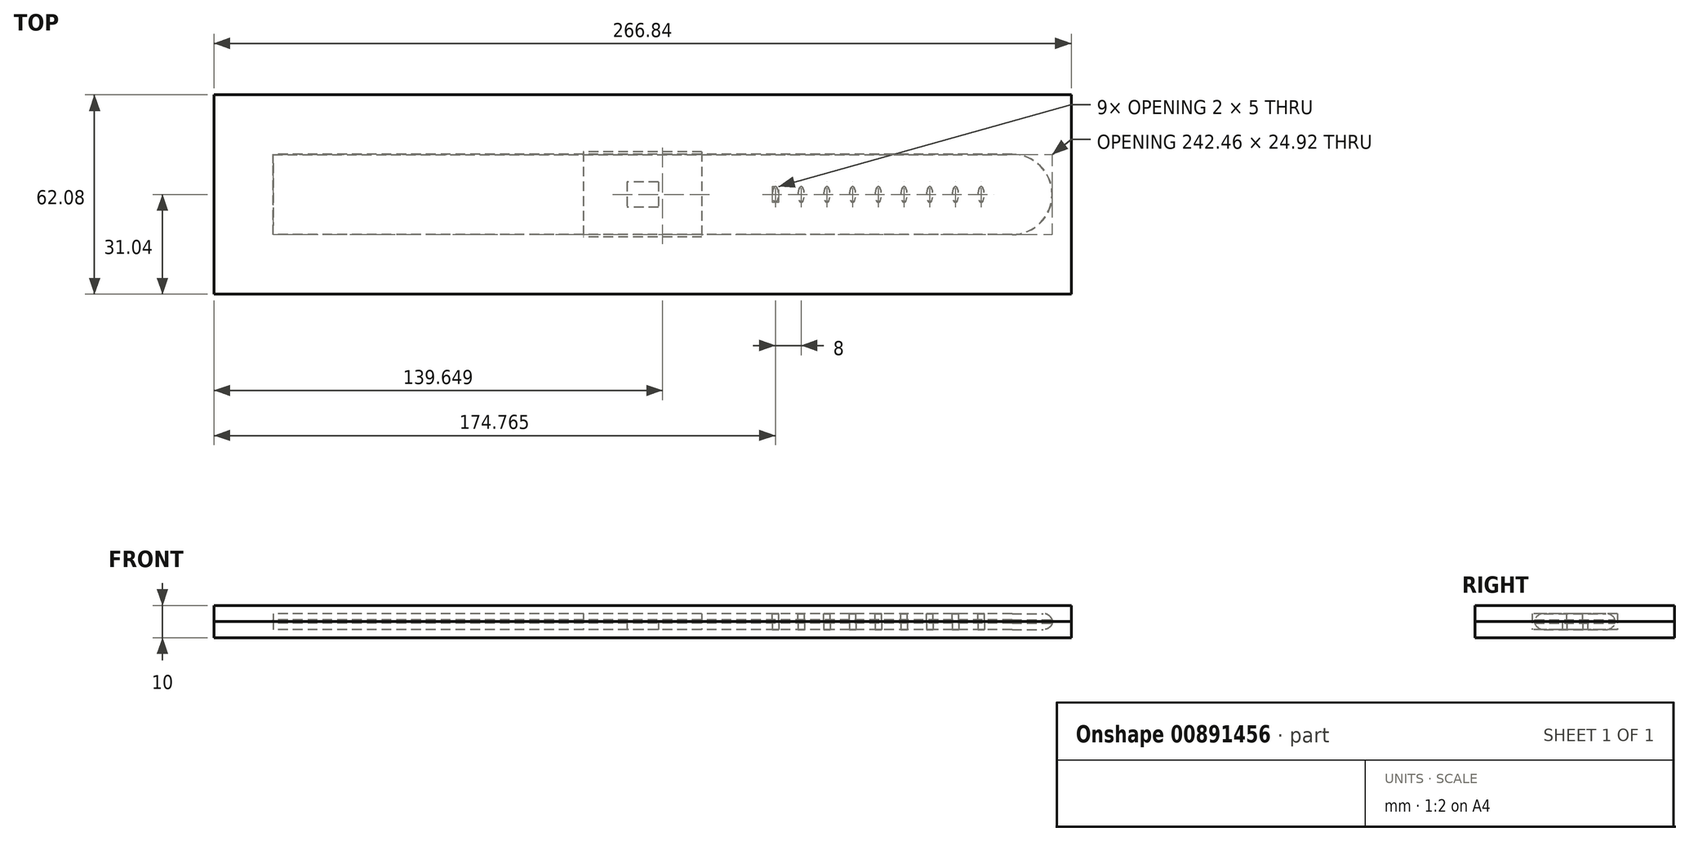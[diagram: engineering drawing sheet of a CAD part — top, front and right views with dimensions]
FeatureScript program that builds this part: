
annotation { "Feature Type Name" : "Feature", "Feature Type Description" : "" }
export const myFeature = defineFeature(function(context is Context, id is Id, definition is map)
    precondition{}
    {
        {
            var Q0;
            Q0=qCreatedBy(makeId("Top.planeOp"),FACE);
            var sketch = newSketch(context, id + "F0", { "sketchPlane" : qUnion([Q0])});
            skLineSegment(sketch, "E0.bottom", {"start": v(4.9, 3.95) * mm, "end": v(-4.9, 3.95) * mm});
            skLineSegment(sketch, "E0.top", {"start": v(4.9, -3.95) * mm, "end": v(-4.9, -3.95) * mm});
            skLineSegment(sketch, "E0.left", {"start": v(4.9, 3.95) * mm, "end": v(4.9, -3.95) * mm});
            skLineSegment(sketch, "E0.right", {"start": v(-4.9, 3.95) * mm, "end": v(-4.9, -3.95) * mm});
            skPoint(sketch, "E0.middle", {"position": v(0, 0) * mm});
            skSolve(sketch);
        }
        {
            var Q0;
            Q0 = qSketchRegion(id + "F0", true);
            extrude(context, id + "F1", {"entities" : qUnion([Q0]), "depth" : 2.4 * mm, "offsetDistance" : 25 * mm});
        }
        {
            var Q0;
            Q0=qCreatedBy(makeId("Top.planeOp"),FACE);
            var sketch = newSketch(context, id + "F2", { "sketchPlane" : qUnion([Q0])});
            skLineSegment(sketch, "E1.bottom", {"start": v(115, 12.5) * mm, "end": v(-115, 12.5) * mm});
            skLineSegment(sketch, "E1.top", {"start": v(115, -12.5) * mm, "end": v(-115, -12.5) * mm});
            skLineSegment(sketch, "E1.left", {"start": v(115, 12.5) * mm, "end": v(115, -12.5) * mm});
            skLineSegment(sketch, "E1.right", {"start": v(-115, 12.5) * mm, "end": v(-115, -12.5) * mm});
            skPoint(sketch, "E1.middle", {"position": v(0, 0) * mm});
            skCircle(sketch, "E2", {"center": v(115, 0) * mm, "radius": 12.5 * mm});
            skEllipse(sketch, "E3", {"center": v(41.34, 0) * mm, "majorRadius": 2.5 * mm, "minorRadius": 1 * mm, "majorAxis": v(0, 1)});
            skEllipse(sketch, "E4", {"center": v(49.34, 0) * mm, "majorRadius": 2.5 * mm, "minorRadius": 1 * mm, "majorAxis": v(0, 1)});
            skEllipse(sketch, "E5", {"center": v(57.34, 0) * mm, "majorRadius": 2.5 * mm, "minorRadius": 1 * mm, "majorAxis": v(0, 1)});
            skEllipse(sketch, "E6", {"center": v(65.34, 0) * mm, "majorRadius": 2.5 * mm, "minorRadius": 1 * mm, "majorAxis": v(0, 1)});
            skEllipse(sketch, "E7", {"center": v(73.34, 0) * mm, "majorRadius": 2.5 * mm, "minorRadius": 1 * mm, "majorAxis": v(0, 1)});
            skEllipse(sketch, "E8", {"center": v(81.34, 0) * mm, "majorRadius": 2.5 * mm, "minorRadius": 1 * mm, "majorAxis": v(0, 1)});
            skEllipse(sketch, "E9", {"center": v(89.34, 0) * mm, "majorRadius": 2.5 * mm, "minorRadius": 1 * mm, "majorAxis": v(0, 1)});
            skEllipse(sketch, "E10", {"center": v(97.34, 0) * mm, "majorRadius": 2.5 * mm, "minorRadius": 1 * mm, "majorAxis": v(0, 1)});
            skEllipse(sketch, "E11", {"center": v(105.34, 0) * mm, "majorRadius": 2.5 * mm, "minorRadius": 1 * mm, "majorAxis": v(0, 1)});
            skSolve(sketch);
        }
        {
            var Q0;
            Q0 = qSketchRegion(id + "F2", true);
            extrude(context, id + "F3", {"entities" : qUnion([Q0]), "depth" : 5 * mm, "offsetDistance" : 25 * mm});
        }
        {
            var Q0;
            Q0=makeQuery(id+"F3.opExtrude","CAP_EDGE",EDGE,{"disambiguationData":[OSD([sQuery(id+"F2.wireOp",EDGE,"E1.top")])],"isStart":false});
            fillet(context, id + "F4", {"entities" : qUnion([Q0]), "radius" : 3 * mm, "tangentPropagation" : true, "allowEdgeOverflow" : false});
        }
        {
            var Q0;
            Q0=makeQuery(id+"F3.opExtrude","CAP_EDGE",EDGE,{"disambiguationData":[OSD([sQuery(id+"F2.wireOp",EDGE,"E1.top")])],"isStart":true});
            fillet(context, id + "F5", {"entities" : qUnion([Q0]), "radius" : 3 * mm, "tangentPropagation" : true, "allowEdgeOverflow" : false});
        }
        {
            var Q0;
            Q0=qCreatedBy(makeId("Top.planeOp"),FACE);
            var sketch = newSketch(context, id + "F6", { "sketchPlane" : qUnion([Q0])});
            skLineSegment(sketch, "E12.bottom", {"start": v(18.45, 13.25) * mm, "end": v(-18.45, 13.25) * mm});
            skLineSegment(sketch, "E12.top", {"start": v(18.45, -13.25) * mm, "end": v(-18.45, -13.25) * mm});
            skLineSegment(sketch, "E12.left", {"start": v(18.45, 13.25) * mm, "end": v(18.45, -13.25) * mm});
            skLineSegment(sketch, "E12.right", {"start": v(-18.45, 13.25) * mm, "end": v(-18.45, -13.25) * mm});
            skPoint(sketch, "E12.middle", {"position": v(0, 0) * mm});
            skSolve(sketch);
        }
        {
            var Q0;
            Q0 = qSketchRegion(id + "F6", true);
            extrude(context, id + "F7", {"entities" : qUnion([Q0]), "depth" : 5 * mm, "offsetDistance" : 25 * mm});
        }
        {
            var Q0;
            Q0=qCreatedBy(makeId("Top.planeOp"),FACE);
            var sketch = newSketch(context, id + "F8", { "sketchPlane" : qUnion([Q0])});
            skLineSegment(sketch, "E13.bottom", {"start": v(133.42, 31.04) * mm, "end": v(-133.42, 31.04) * mm});
            skLineSegment(sketch, "E13.top", {"start": v(133.42, -31.04) * mm, "end": v(-133.42, -31.04) * mm});
            skLineSegment(sketch, "E13.left", {"start": v(133.42, 31.04) * mm, "end": v(133.42, -31.04) * mm});
            skLineSegment(sketch, "E13.right", {"start": v(-133.42, 31.04) * mm, "end": v(-133.42, -31.04) * mm});
            skPoint(sketch, "E13.middle", {"position": v(0, 0) * mm});
            skSolve(sketch);
        }
        {
            var Q0;
            Q0 = qSketchRegion(id + "F8", true);
            extrude(context, id + "F9", {"entities" : qUnion([Q0]), "depth" : 2.5 * mm, "offsetDistance" : 25 * mm, "hasSecondDirection" : true, "secondDirectionOppositeDirection" : false, "secondDirectionDepth" : -2.5 * mm});
        }
        {
            var Q0;
            Q0=makeQuery(id+"F3.opExtrude","SWEPT_BODY",BODY,{"disambiguationData":[OSD([sQuery(id+"F2.wireOp",EDGE,"E1.bottom"),sQuery(id+"F2.wireOp",EDGE,"E1.top"),sQuery(id+"F2.wireOp",EDGE,"E1.right"),sQuery(id+"F2.wireOp",EDGE,"E2"),sQuery(id+"F2.wireOp",EDGE,"E3"),sQuery(id+"F2.wireOp",EDGE,"E4"),sQuery(id+"F2.wireOp",EDGE,"E5"),sQuery(id+"F2.wireOp",EDGE,"E6"),sQuery(id+"F2.wireOp",EDGE,"E7"),sQuery(id+"F2.wireOp",EDGE,"E8"),sQuery(id+"F2.wireOp",EDGE,"E9"),sQuery(id+"F2.wireOp",EDGE,"E10"),sQuery(id+"F2.wireOp",EDGE,"E11")])]});
            var Q1;
            Q1=makeQuery(id+"F9.opExtrude","SWEPT_BODY",BODY,{"disambiguationData":[OSD([sQuery(id+"F8.wireOp",EDGE,"E13.bottom"),sQuery(id+"F8.wireOp",EDGE,"E13.top"),sQuery(id+"F8.wireOp",EDGE,"E13.left"),sQuery(id+"F8.wireOp",EDGE,"E13.right")])]});
            booleanBodies(context, id + "F10", {"operationType" : BooleanOperationType.SUBTRACTION, "tools" : qUnion([Q0]), "targets" : qUnion([Q1])});
        }
        {
            var Q0;
            Q0=makeQuery(id+"F9.opExtrude","SWEPT_BODY",BODY,{"disambiguationData":[OSD([sQuery(id+"F8.wireOp",EDGE,"E13.bottom"),sQuery(id+"F8.wireOp",EDGE,"E13.top"),sQuery(id+"F8.wireOp",EDGE,"E13.left"),sQuery(id+"F8.wireOp",EDGE,"E13.right")])]});
            var Q1;
            Q1=makeQuery(id+"F9.opExtrude","CAP_EDGE",EDGE,{"disambiguationData":[OSD([sQuery(id+"F8.wireOp",EDGE,"E13.top")])],"isStart":false});
            transform(context, id + "F11", {"entities" : qUnion([Q0]), "transformType" : TransformType.TRANSLATION_3D, "dx" : 0 * mm, "dy" : 0 * mm, "dz" : 0 * mm, "makeCopy" : true});
        }
        {
            var Q0;
            Q0=makeQuery(id+"F9.opExtrude","SWEPT_BODY",BODY,{"disambiguationData":[OSD([sQuery(id+"F8.wireOp",EDGE,"E13.bottom"),sQuery(id+"F8.wireOp",EDGE,"E13.top"),sQuery(id+"F8.wireOp",EDGE,"E13.left"),sQuery(id+"F8.wireOp",EDGE,"E13.right")])]});
            var Q1;
            Q1=qCreatedBy(makeId("Top.planeOp"),FACE);
            mirror(context, id + "F12", {"entities" : qUnion([Q0]), "mirrorPlane" : qUnion([Q1])});
        }
        {
            var Q0;
            Q0=makeQuery(id+"F12.opPattern","COPY",BODY,{"derivedFrom":makeQuery(id+"F9.opExtrude","SWEPT_BODY",BODY,{"disambiguationData":[OSD([sQuery(id+"F8.wireOp",EDGE,"E13.bottom"),sQuery(id+"F8.wireOp",EDGE,"E13.top"),sQuery(id+"F8.wireOp",EDGE,"E13.left"),sQuery(id+"F8.wireOp",EDGE,"E13.right")])]}),"instanceName":"1"});
            transform(context, id + "F13", {"entities" : qUnion([Q0]), "transformType" : TransformType.TRANSLATION_3D, "dx" : 0 * mm, "dy" : 0 * mm, "dz" : 5 * mm, "makeCopy" : false});
        }
    });
